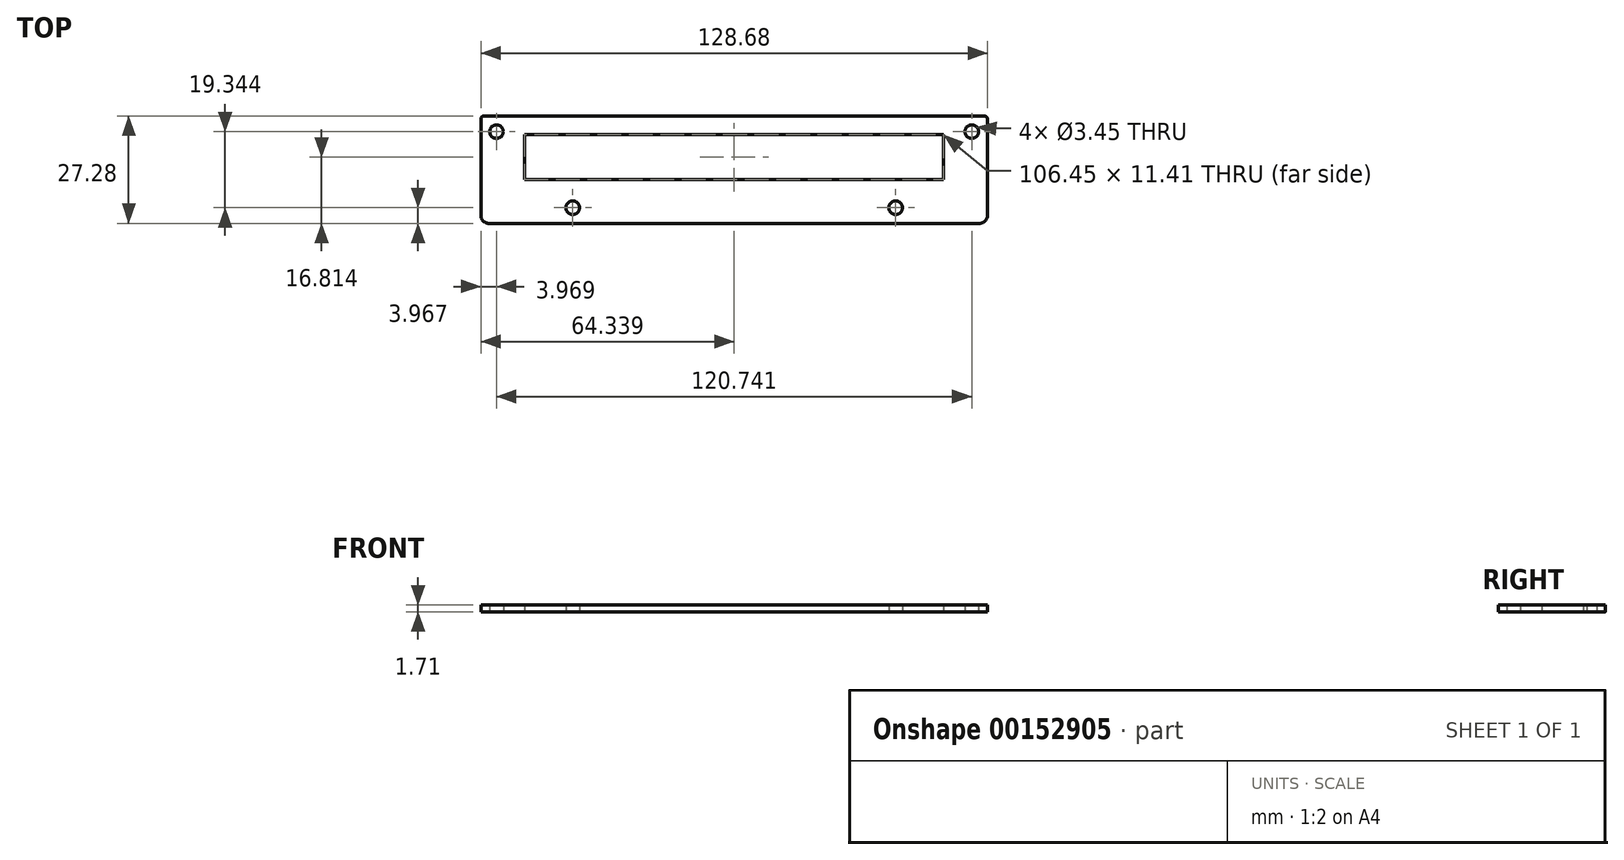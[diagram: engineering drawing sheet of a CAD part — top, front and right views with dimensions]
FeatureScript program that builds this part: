
annotation { "Feature Type Name" : "Feature", "Feature Type Description" : "" }
export const myFeature = defineFeature(function(context is Context, id is Id, definition is map)
    precondition{}
    {
        {
            var Q0;
            Q0=qCreatedBy(makeId("Top.planeOp"),FACE);
            var sketch = newSketch(context, id + "F0", { "sketchPlane" : qUnion([Q0])});
            skLineSegment(sketch, "E0.bottom", {"start": v(0, 0) * mm, "end": v(128.68, 0) * mm});
            skLineSegment(sketch, "E0.top", {"start": v(0, -27.28) * mm, "end": v(128.68, -27.28) * mm});
            skLineSegment(sketch, "E0.left", {"start": v(0, 0) * mm, "end": v(0, -27.28) * mm});
            skLineSegment(sketch, "E0.right", {"start": v(128.68, 0) * mm, "end": v(128.68, -27.28) * mm});
            skLineSegment(sketch, "E1", {"start": v(0, -3.97) * mm, "end": v(3.97, -3.97) * mm, "construction": true});
            skLineSegment(sketch, "E2", {"start": v(3.97, -3.97) * mm, "end": v(3.97, 0) * mm, "construction": true});
            skLineSegment(sketch, "E3", {"start": v(124.71, 0) * mm, "end": v(124.71, -3.97) * mm, "construction": true});
            skLineSegment(sketch, "E4", {"start": v(124.71, -3.97) * mm, "end": v(128.68, -3.97) * mm, "construction": true});
            skLineSegment(sketch, "E5", {"start": v(64.34, -27.28) * mm, "end": v(64.34, -23.31) * mm, "construction": true});
            skLineSegment(sketch, "E6", {"start": v(64.34, -23.31) * mm, "end": v(105.37, -23.31) * mm, "construction": true});
            skLineSegment(sketch, "E7", {"start": v(64.34, -23.31) * mm, "end": v(23.31, -23.31) * mm, "construction": true});
            skCircle(sketch, "E8", {"center": v(3.97, -3.97) * mm, "radius": 1.73 * mm});
            skCircle(sketch, "E9", {"center": v(23.31, -23.31) * mm, "radius": 1.73 * mm});
            skCircle(sketch, "E10", {"center": v(105.37, -23.31) * mm, "radius": 1.73 * mm});
            skCircle(sketch, "E11", {"center": v(124.71, -3.97) * mm, "radius": 1.73 * mm});
            skLineSegment(sketch, "E12", {"start": v(64.34, -23.31) * mm, "end": v(64.34, -16.17) * mm, "construction": true});
            skLineSegment(sketch, "E13", {"start": v(64.34, 0) * mm, "end": v(64.34, -4.76) * mm, "construction": true});
            skLineSegment(sketch, "E14.bottom", {"start": v(117.57, -16.17) * mm, "end": v(11.11, -16.17) * mm});
            skLineSegment(sketch, "E14.top", {"start": v(117.57, -4.76) * mm, "end": v(11.11, -4.76) * mm});
            skLineSegment(sketch, "E14.left", {"start": v(117.57, -16.17) * mm, "end": v(117.57, -4.76) * mm});
            skLineSegment(sketch, "E14.right", {"start": v(11.11, -16.17) * mm, "end": v(11.11, -4.76) * mm});
            skLineSegment(sketch, "E15", {"start": v(124.71, -3.97) * mm, "end": v(117.57, -3.97) * mm, "construction": true});
            skLineSegment(sketch, "E16", {"start": v(117.57, -4.76) * mm, "end": v(117.57, -3.97) * mm, "construction": true});
            skLineSegment(sketch, "E17", {"start": v(3.97, -3.97) * mm, "end": v(23.31, -3.97) * mm, "construction": true});
            skLineSegment(sketch, "E18", {"start": v(23.31, -3.97) * mm, "end": v(23.31, -23.31) * mm, "construction": true});
            skSolve(sketch);
        }
        {
            var Q0;
            Q0=qSketchRegion(id+"F0",true);
            extrude(context, id + "F1", {"entities" : qUnion([Q0]), "depth" : 1.7 * mm});
        }
        {
            var Q0;
            Q0=makeQuery(id+"F1.opExtrude","SWEPT_EDGE",EDGE,{"disambiguationData":[OSD([sQuery(id+"F0.wireOp",EDGE,"E0.top"),sQuery(id+"F0.wireOp",EDGE,"E0.left")])]});
            var Q1;
            Q1=makeQuery(id+"F1.opExtrude","SWEPT_EDGE",EDGE,{"disambiguationData":[OSD([sQuery(id+"F0.wireOp",EDGE,"E0.top"),sQuery(id+"F0.wireOp",EDGE,"E0.right")])]});
            fillet(context, id + "F2", {"entities" : qUnion([Q0, Q1]), "radius" : 1.98 * mm, "tangentPropagation" : true, "allowEdgeOverflow" : false});
        }
        {
            var Q0;
            Q0=makeQuery(id+"F1.opExtrude","SWEPT_EDGE",EDGE,{"disambiguationData":[OSD([sQuery(id+"F0.wireOp",EDGE,"E0.bottom"),sQuery(id+"F0.wireOp",EDGE,"E0.left")])]});
            var Q1;
            Q1=makeQuery(id+"F1.opExtrude","SWEPT_EDGE",EDGE,{"disambiguationData":[OSD([sQuery(id+"F0.wireOp",EDGE,"E0.bottom"),sQuery(id+"F0.wireOp",EDGE,"E0.right")])]});
            fillet(context, id + "F3", {"entities" : qUnion([Q0, Q1]), "radius" : 0.76 * mm, "tangentPropagation" : true, "allowEdgeOverflow" : false});
        }
    });
